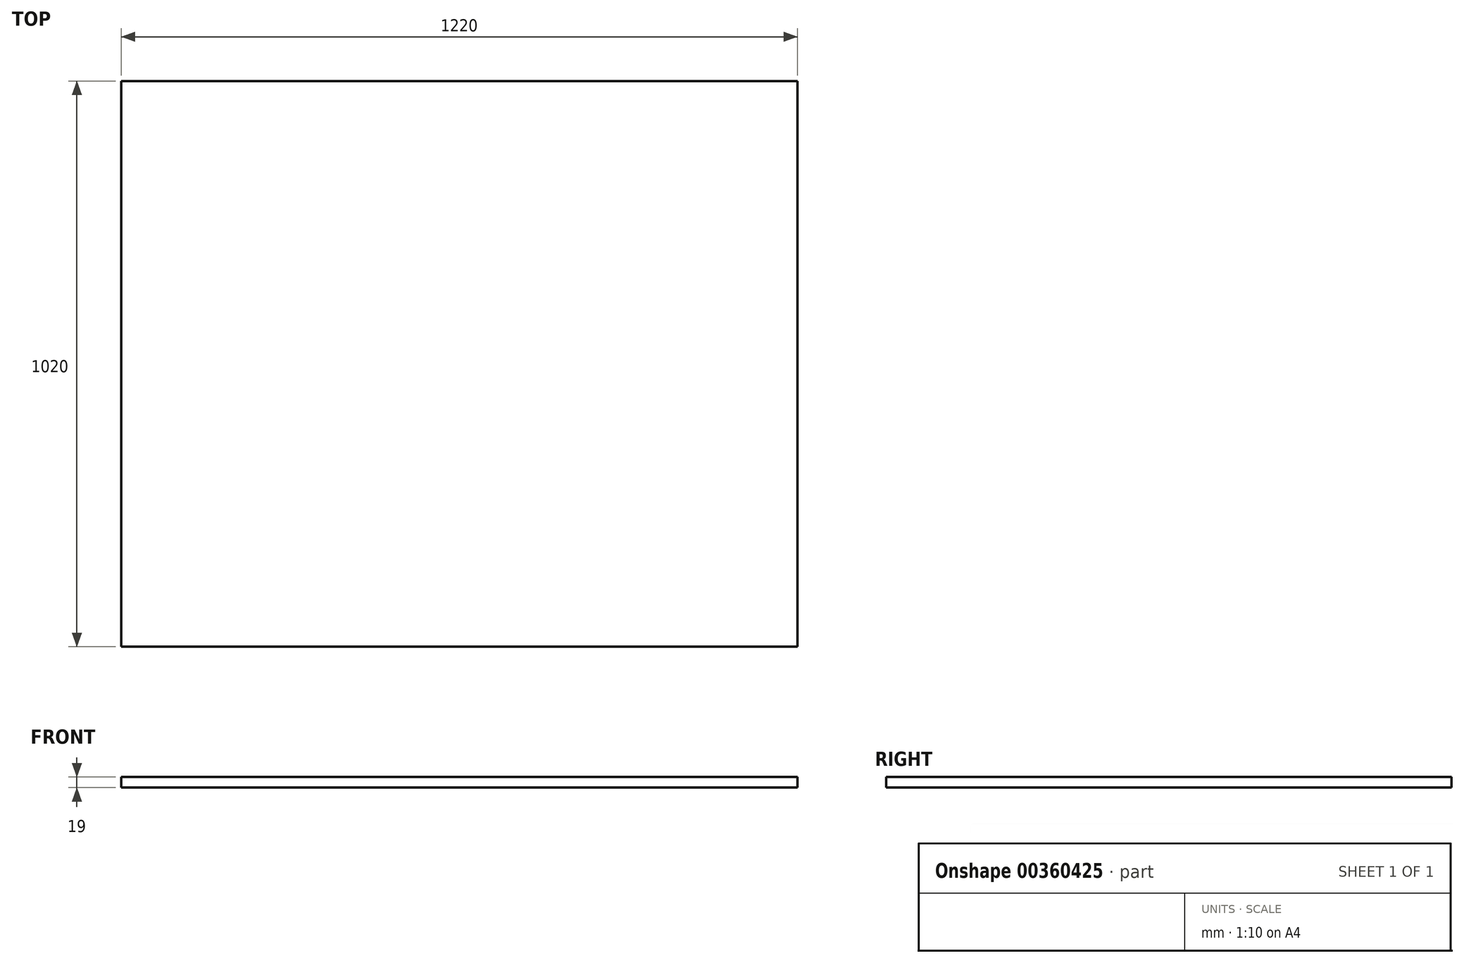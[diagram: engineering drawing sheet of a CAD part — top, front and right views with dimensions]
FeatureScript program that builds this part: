
annotation { "Feature Type Name" : "Feature", "Feature Type Description" : "" }
export const myFeature = defineFeature(function(context is Context, id is Id, definition is map)
    precondition{}
    {
        {
            var Q0;
            Q0=qCreatedBy(makeId("Top.planeOp"),FACE);
            var sketch = newSketch(context, id + "F0", { "sketchPlane" : qUnion([Q0])});
            skLineSegment(sketch, "E0.bottom", {"start": v(1220, 1020) * mm, "end": v(0, 1020) * mm});
            skLineSegment(sketch, "E0.top", {"start": v(1220, 0) * mm, "end": v(0, 0) * mm});
            skLineSegment(sketch, "E0.left", {"start": v(1220, 1020) * mm, "end": v(1220, 0) * mm});
            skLineSegment(sketch, "E0.right", {"start": v(0, 1020) * mm, "end": v(0, 0) * mm});
            skSolve(sketch);
        }
        {
            var Q0;
            Q0=makeQuery(id+"F0.imprint","IMPRINT",FACE,{"disambiguationData":[TD([[makeQuery(id+"F0.imprint","IMPRINT",EDGE,{"derivedFrom":sQuery(id+"F0.wireOp",EDGE,"E0.bottom")}),1.0]])]});
            extrude(context, id + "F1", {"entities" : qUnion([Q0]), "depth" : 19 * mm});
        }
    });
